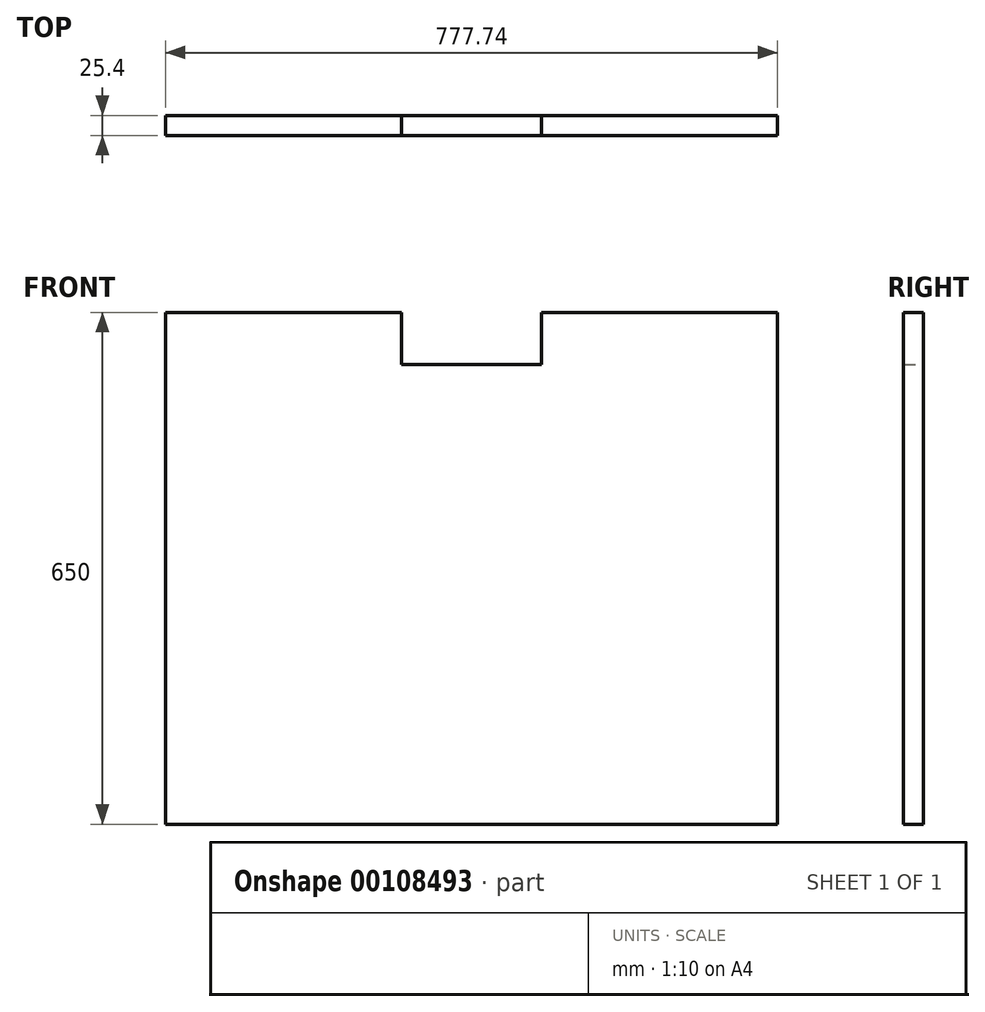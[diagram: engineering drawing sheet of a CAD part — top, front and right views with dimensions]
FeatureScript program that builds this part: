
annotation { "Feature Type Name" : "Feature", "Feature Type Description" : "" }
export const myFeature = defineFeature(function(context is Context, id is Id, definition is map)
    precondition{}
    {
        {
            var Q0;
            Q0=qCreatedBy(makeId("Front.planeOp"),FACE);
            var sketch = newSketch(context, id + "F0", { "sketchPlane" : qUnion([Q0])});
            skLineSegment(sketch, "E0.bottom", {"start": v(388.87, 325) * mm, "end": v(-388.87, 325) * mm});
            skLineSegment(sketch, "E0.top", {"start": v(388.87, -325) * mm, "end": v(-388.87, -325) * mm});
            skLineSegment(sketch, "E0.left", {"start": v(388.87, 325) * mm, "end": v(388.87, -325) * mm});
            skLineSegment(sketch, "E0.right", {"start": v(-388.87, 325) * mm, "end": v(-388.87, -325) * mm});
            skPoint(sketch, "E0.middle", {"position": v(0, 0) * mm});
            skLineSegment(sketch, "E1.bottom", {"start": v(88.76, 391.24) * mm, "end": v(-88.76, 391.24) * mm});
            skLineSegment(sketch, "E1.top", {"start": v(88.76, 258.76) * mm, "end": v(-88.76, 258.76) * mm});
            skLineSegment(sketch, "E1.left", {"start": v(88.76, 391.24) * mm, "end": v(88.76, 258.76) * mm});
            skLineSegment(sketch, "E1.right", {"start": v(-88.76, 391.24) * mm, "end": v(-88.76, 258.76) * mm});
            skPoint(sketch, "E1.middle", {"position": v(0, 325) * mm});
            skSolve(sketch);
        }
        {
            var Q0;
            Q0=makeQuery(id+"F0.imprint","IMPRINT",FACE,{"disambiguationData":[TD([[makeQuery(id+"F0.imprint","IMPRINT",EDGE,{"derivedFrom":sQuery(id+"F0.wireOp",EDGE,"E0.top")}),-1.0]])]});
            extrude(context, id + "F1", {"entities" : qUnion([Q0]), "depth" : 25.4 * mm});
        }
    });
